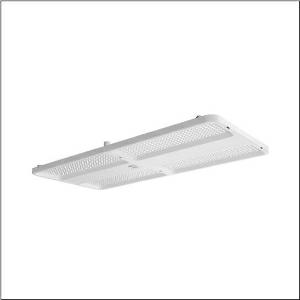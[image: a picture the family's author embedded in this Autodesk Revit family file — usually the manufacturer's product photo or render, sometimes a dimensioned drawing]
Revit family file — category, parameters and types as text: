
# Revit family: highbay_21_maxi_52hn12db4mda01
name_source: partatom
category: Lighting Fixtures
units: mm (PartAtom-declared; Revit-internal decimal feet)

## family parameters
Cut with Voids When Loaded = No
Host = Face
Light Source = No
Part Type = Normal
Room Calculation Point = No
Round Connector Dimension = Use Diameter
Shared = No

## types (1)
- --- (1 x LED, 28000 lm, 144.5 W, 4000K)
    Apparent Load = 144 VA
    CIE Flux Codes = 90 98 100 100 100
    Color Rendering = 80
    Color Temperature = 4000K
    Default Elevation = 1800 mm
    Description = high bay luminaire Highbay 21 maxi; direct symmetric wide distribution, light control with lens of PMMA; UGR ≤ 22 (X = 4H | Y = 8H | S = 0.25H | reflection values 70/50/20); luminous flux: 28.000lm; light colour: 840, colour temperature: 4000K, MacAdam ≤ 3 SDCM (initial), colour rendering: CRI > 80; luminous efficacy: 193,8lm/W; rated service life: 75.000h (L80/B50) at AT= ta max; control: Bluetooth® Mesh; for wireless networking: Node multi-sensor luminaire for setting up a local control solution without a higher-level application controller, intelligence completely integrated into the luminaire; with auto-swarm function: leading lighting creates safety. The function is already active without any „out-of-the-box“ commissioning; commissioning is not necessary thanks to „out-of-the-box“ functions: basic functions (presence lighting, follow-up times, fading times, etc.) are already preset at the factory; no control line such as DALI between the Node multi-sensor luminaires and Nodes is required, wireless integration of other Node luminaires and Node multi-sensor luminaires into the network is possible; number of Node multi-sensor luminaires in the project can be expanded as required, network sizes > 300 Nodes can be realized; can also be connected to lighting or building automation via various gateways upon request; integrated DALI2 ECG provides luminaire data (according to IEC62386, Part 251), energy data (Part 252), and monitoring and analytics data (Part 253) to higher-level systems for further processing; luminaire with PIR sensor (passive-infrared); with light sensor; luminaire connection: terminal, 5-pole, max. 2.5mm² (cable entry for one cable, Ø 8.5..16mm); mains connection: 230..240V, AC 50/60Hz; connected load: 144,5W; protection rating (complete): IP65; insulation class (complete): insulation class I (protective earthing); protection symbol: D; certification: CE, ENEC, VDE, UKCA; internal wiring halogen-free; luminaire corresponds to IFS (International Featured Standards) requirements for safety and quality in the food industry; LABS conformity tested according to VDMA 24364:2018-05; housing frame of high-performance plastic PA6, matt traffic white (RAL 9016); cover of PMMA; dimension (LxWxH): 946 x 442 x 72mm; permissible operating ambient temperature: -20..+45°C (reducing of maximum allowable ambient temperature of 5°C with ceiling mounting); packaging unit: 1 piece; (delivery without accessories; please order mounting accessories separately)
    Height = 72 mm  [stored 0.23622 ft]
    Lamp = 1 x LED
    Lamp Light Flux = 28000 lm
    Lamp Power = 144.5 W
    Lamp count = 1
    Length = 946 mm
    Luminous efficacy = 194 lm/W
    Manufacturer = Siteco
    ModVariant = No
    Model = 52HN12DB4MDA01
    Mounting Place = Ceiling
    Mounting Type = Pendant
    Number of Poles = 1
    OnlyDefault = Yes
    Power Factor = 1
    Product Name = Highbay 21 maxi
    Product group = high bay luminaire
    ProductGroupID = 901
    Protection Class = Protection class I
    Protection Degree = IP 65
    RLX_Detail_Level = 1
    RLX_Emergency_Light_Flux = 0 lm
    RLX_Emergency_Type = 0
    RLX_Emergency_Type_DB = No
    RlxData = <blob elided: 128909 chars, md5=e04ffeea>
    Socket = socket
    Standby Power = 0 W
    System Light Flux = 28000 lm
    System Power = 144 W
    Type Comments = factory setting: luminous flux: 100 % | dim-lin: 254 | 668 mA
    Type Image = l_1363267.jpg
    URL = http://relux.com
    VarID = @adj_012081
    Voltage = 0 V
    Weight = 0.00 kg
    Width = 442 mm

note: [stored X ft] marks values corroborated as IEEE doubles in the binary element streams (Revit-internal decimal feet)

## geometry (parser evidence)
native form markers: Blend x4, Sweep x10
no freeform markers — native parametric forms only
